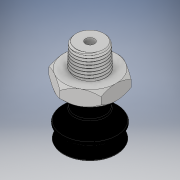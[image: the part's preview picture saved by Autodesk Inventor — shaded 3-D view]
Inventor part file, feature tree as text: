
AUTODESK INVENTOR PART (.ipt)
format: ipt  version: 2019.4 (Build 234330000, 330)  size: 749,056 bytes
history: native  units: mm
features: revolve x1, boolean_combine x1
ambient origin geometry x8: Origin, YZ Plane, XZ Plane, XY Plane, X Axis, Y Axis, Z Axis, Center Point
bodies: Solid1 (feature_tree), Solid2 (feature_tree)
feature tree (2):
  revolve  "Revolve1"  [1 undecoded]
  boolean_combine  "Combine1"
note: 1 required parameter value undecoded (feature->parameter linkage not recoverable at this tier; creation-order binding heuristic only, values carry confidence <= 0.55)
